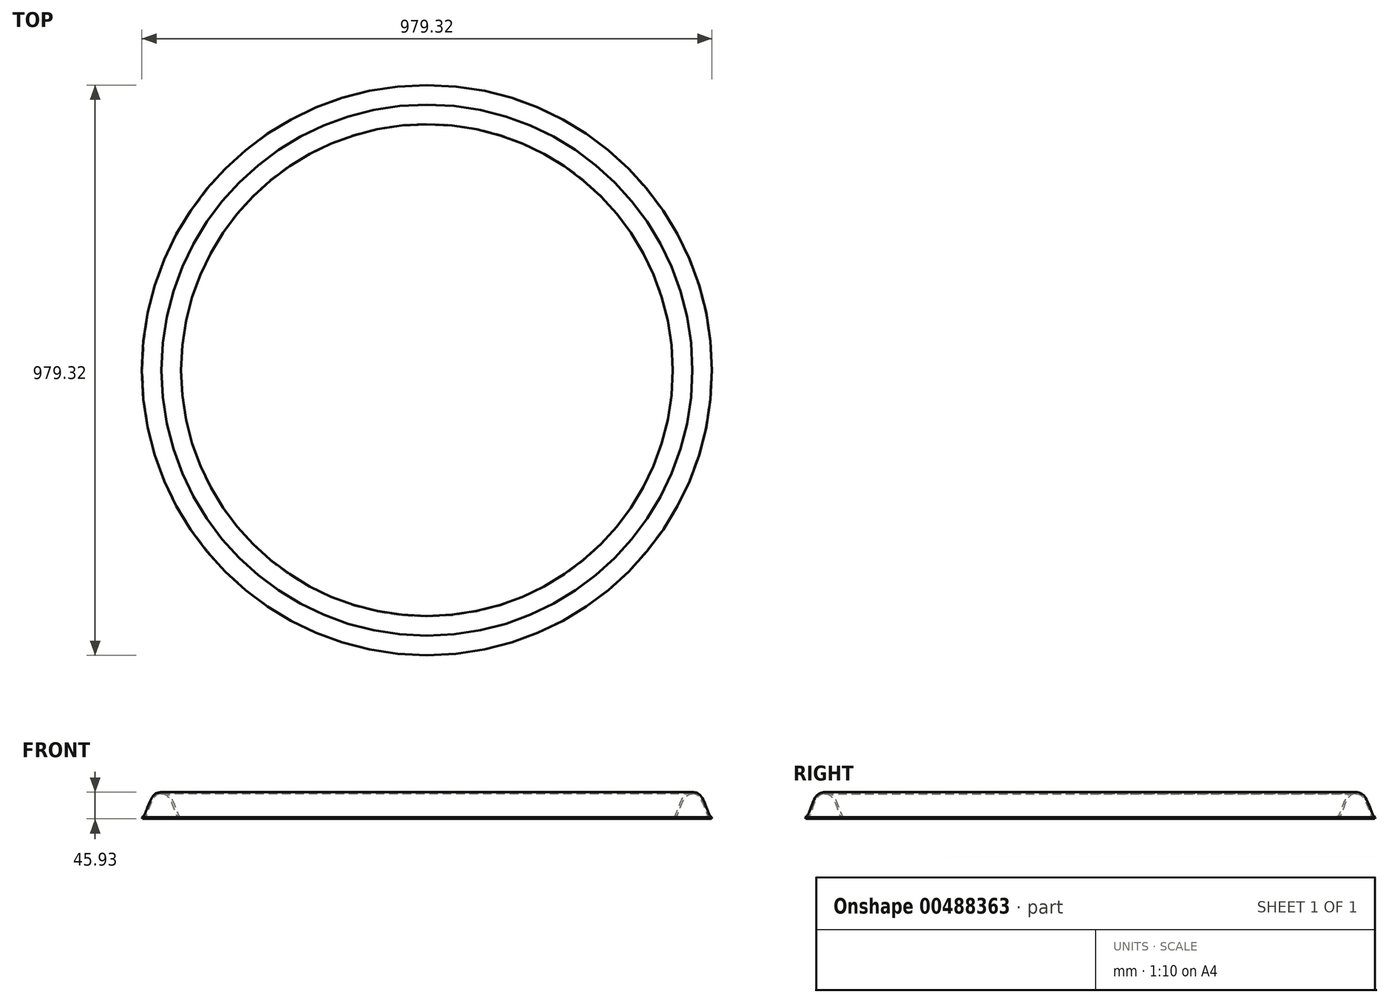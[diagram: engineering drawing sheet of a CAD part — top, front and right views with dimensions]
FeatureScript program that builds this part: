
annotation { "Feature Type Name" : "Feature", "Feature Type Description" : "" }
export const myFeature = defineFeature(function(context is Context, id is Id, definition is map)
    precondition{}
    {
        {
            var Q0;
            Q0=qCreatedBy(makeId("Front.planeOp"),FACE);
            var sketch = newSketch(context, id + "F0", { "sketchPlane" : qUnion([Q0])});
            skFitSpline(sketch, "E0", {"points": [v(-33.67, -10.75) * mm, v(-27.3, -2.63) * mm, v(-13.02, 27.17) * mm, v(0, 32.18) * mm], "startDerivative": vector(40.06, 13.77) * mm, "endDerivative": vector(43.4, 4.56) * mm});
            skFitSpline(sketch, "E1.MirrorCS", {"points": [v(33.67, -10.75) * mm, v(27.3, -2.63) * mm, v(13.02, 27.17) * mm, v(0, 32.18) * mm], "startDerivative": vector(-40.06, 13.77) * mm, "endDerivative": vector(-43.4, 4.56) * mm});
            skFitSpline(sketch, "E2.0", {"points": [v(-32.64, -13.75) * mm, v(-32.1, -13.56) * mm, v(-31.05, -13.12) * mm, v(-29.61, -12.24) * mm, v(-28.36, -11.15) * mm, v(-27.32, -9.91) * mm, v(-26.47, -8.57) * mm, v(-25.73, -7.14) * mm, v(-25.06, -5.62) * mm, v(-24.4, -3.97) * mm, v(-23.72, -2.16) * mm, v(-22.75, 0.46) * mm, v(-21.44, 4.05) * mm, v(-19.7, 8.63) * mm, v(-17.79, 13.23) * mm, v(-15.74, 17.59) * mm, v(-13.94, 20.79) * mm, v(-12.47, 22.94) * mm, v(-11.56, 24.09) * mm, v(-10.85, 24.86) * mm, v(-10.15, 25.55) * mm, v(-8.92, 26.56) * mm, v(-7.14, 27.56) * mm, v(-4.85, 28.3) * mm, v(-2.36, 28.74) * mm, v(-0.58, 28.93) * mm, v(0.33, 29.02) * mm]});
            skLineSegment(sketch, "E3", {"start": v(-33.67, -10.75) * mm, "end": v(-32.64, -13.75) * mm});
            skFitSpline(sketch, "E4.0", {"points": [v(32.64, -13.75) * mm, v(32.1, -13.56) * mm, v(31.05, -13.12) * mm, v(29.61, -12.24) * mm, v(28.36, -11.15) * mm, v(27.32, -9.91) * mm, v(26.47, -8.57) * mm, v(25.73, -7.14) * mm, v(25.06, -5.62) * mm, v(24.4, -3.97) * mm, v(23.72, -2.16) * mm, v(22.75, 0.46) * mm, v(21.44, 4.05) * mm, v(19.7, 8.63) * mm, v(17.79, 13.23) * mm, v(15.74, 17.59) * mm, v(13.94, 20.79) * mm, v(12.47, 22.94) * mm, v(11.56, 24.09) * mm, v(10.85, 24.86) * mm, v(10.15, 25.55) * mm, v(8.92, 26.56) * mm, v(7.14, 27.56) * mm, v(4.85, 28.3) * mm, v(2.36, 28.74) * mm, v(0.58, 28.93) * mm, v(-0.33, 29.02) * mm]});
            skLineSegment(sketch, "E5", {"start": v(32.64, -13.75) * mm, "end": v(33.67, -10.75) * mm});
            skLineSegment(sketch, "E6", {"start": v(455.99, 131.07) * mm, "end": v(455.99, -169.92) * mm, "construction": true});
            skSolve(sketch);
        }
        {
            var Q0;
            Q0=makeQuery(id+"F0.imprint","IMPRINT",FACE,{"disambiguationData":[TD([[makeQuery(id+"F0.imprint","IMPRINT",EDGE,{"derivedFrom":sQuery(id+"F0.wireOp",EDGE,"E0")}),-1.0]])]});
            var Q1;
            Q1=sQuery(id+"F0.wireOp",EDGE,"E6");
            revolve(context, id + "F1", {"entities" : qUnion([Q0]), "axis" : qUnion([Q1]), "revolveType" : RevolveType.FULL});
        }
    });
